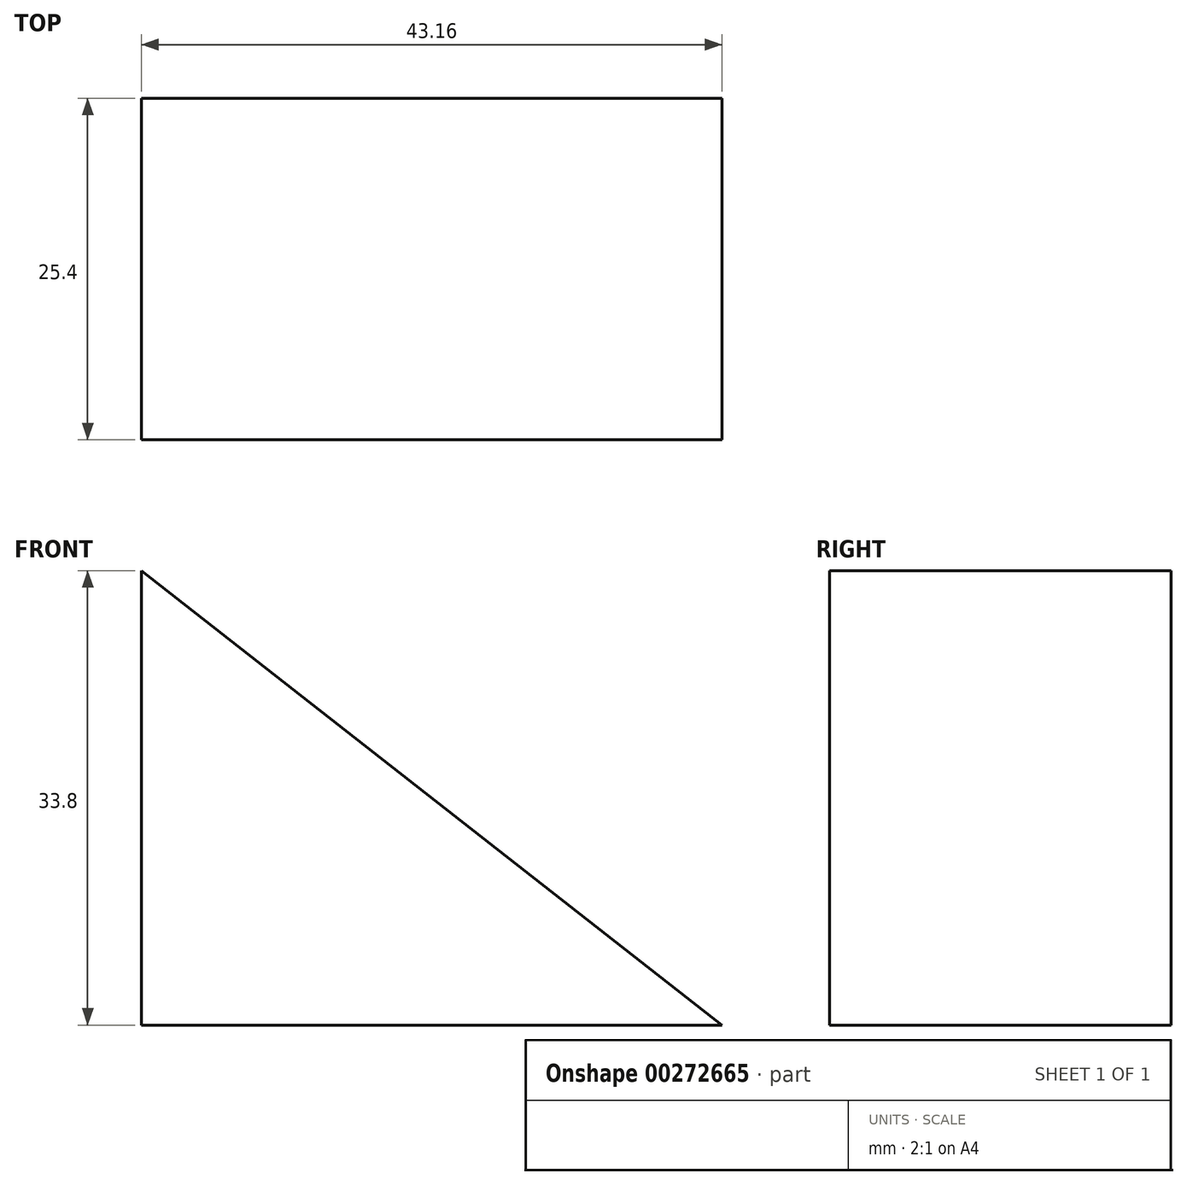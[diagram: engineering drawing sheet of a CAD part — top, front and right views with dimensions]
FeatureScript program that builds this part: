
annotation { "Feature Type Name" : "Feature", "Feature Type Description" : "" }
export const myFeature = defineFeature(function(context is Context, id is Id, definition is map)
    precondition{}
    {
        {
            var Q0;
            Q0=qCreatedBy(makeId("Front.planeOp"),FACE);
            var sketch = newSketch(context, id + "F0", { "sketchPlane" : qUnion([Q0])});
            skLineSegment(sketch, "E0", {"start": v(0, 0) * mm, "end": v(-43.16, 0) * mm});
            skLineSegment(sketch, "E1", {"start": v(-43.16, 0) * mm, "end": v(-43.16, 33.8) * mm});
            skLineSegment(sketch, "E2", {"start": v(-43.16, 33.8) * mm, "end": v(0, 0) * mm});
            skLineSegment(sketch, "E3", {"start": v(-19.9, 15.58) * mm, "end": v(-29.98, 8.21) * mm});
            skSolve(sketch);
        }
        {
            var Q0;
            {var subQ0=sQuery(id+"F0.wireOp",EDGE,"E0");Q0=makeQuery(id+"F0.imprint","IMPRINT",FACE,{"disambiguationData":[TD([[makeQuery(id+"F0.imprint","IMPRINT",EDGE,{"derivedFrom":subQ0}),-1.0]])]});}
            extrude(context, id + "F1", {"entities" : qUnion([Q0]), "depth" : 25.4 * mm});
        }
    });
